# Revit family: Flushometer-Toilet_Manual-KOHLER-Primme-K-76321
name_source: partatom
category: Plumbing Fixtures
revit_build: Autodesk Revit 2015 (Build: 20140606_1530(x64)
units: mm (PartAtom-declared; Revit-internal decimal feet)

## types (1)
- CP-Polished Chrome
    ADA Compliant = Yes
    Assembly Code = D2020
    CW Connection = Yes
    Cold Water Inlet = Cold Water Inlet
    Cold Water Outlet = Cold Water Outlet
    Date Modified = 03/11/2019
    Default Elevation = 0"
    Description = Manual flushometer valve for 1.28 gpf toilet
    Finish = Kohler-Metal-CP-Polished_Chrome
    Flow Rate = 25 GPM
    Flush Rate = 1.28 GPF
    HW Connection = No
    Hot Water Inlet = Hot Water Inlet
    Manufacturer = KOHLER Co.
    MasterFormat 1995 = 154300
    MasterFormat 2004 = 22.11.00
    Material = Durable Brass Construction
    Model = K-76321-CP
    Pressure = 80.00 psi
    Product Documentation Link = https://www.us.kohler.com
    Product Name = Primme
    Product Page URL = http://www.us.kohler.com
    URL = https://www.us.kohler.com
    Vent Connection = No
    Waste Connection = No
    WaterSense Certified = Yes

## geometry (parser evidence)
native form markers: Sweep x5
no freeform markers — native parametric forms only
